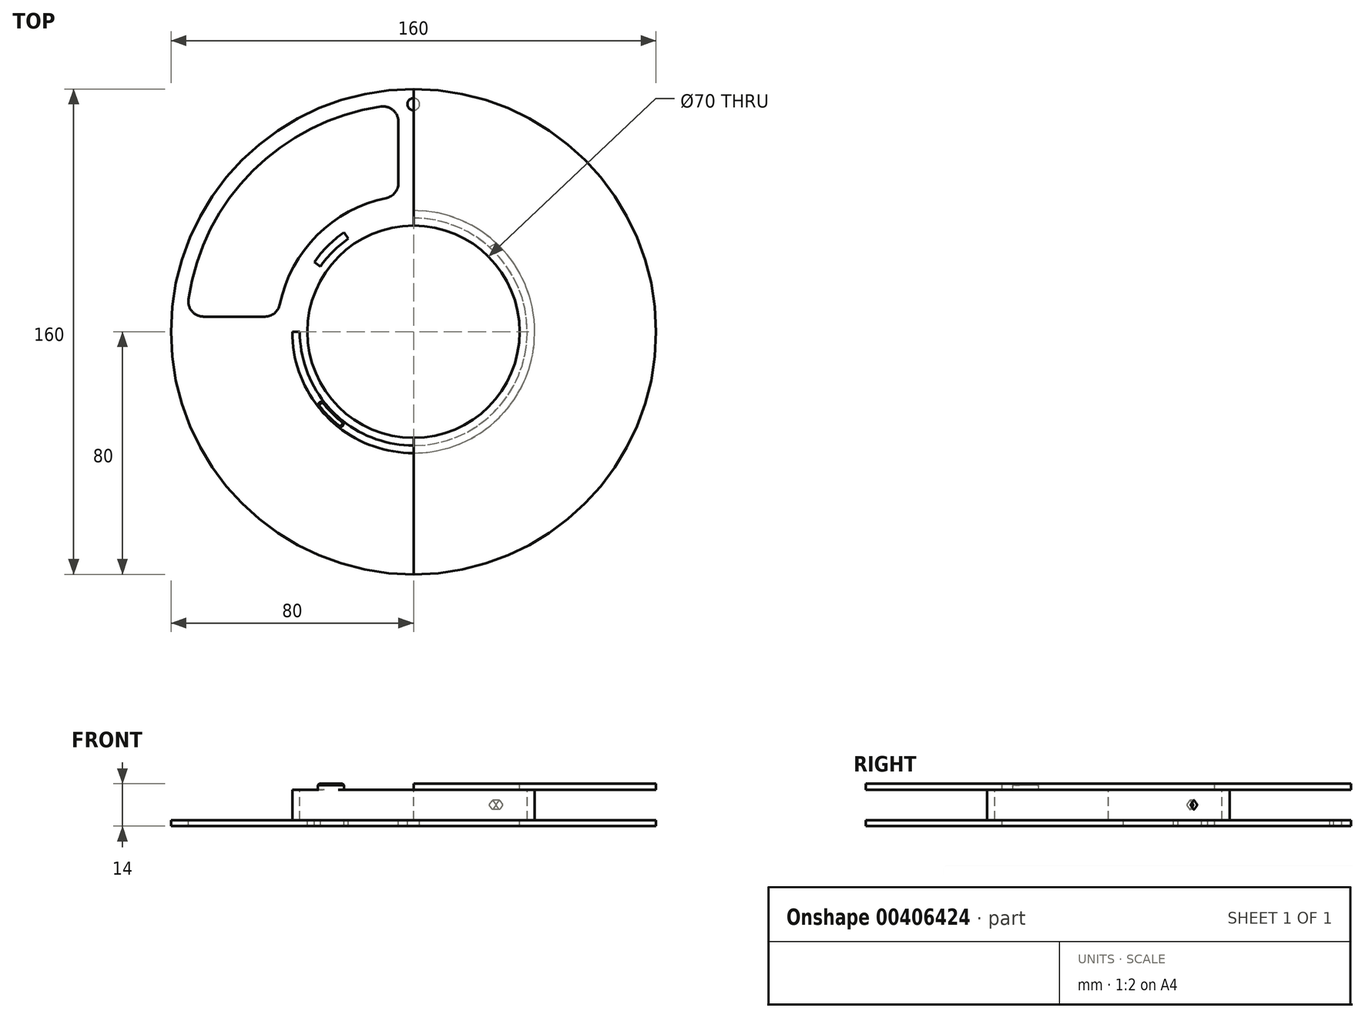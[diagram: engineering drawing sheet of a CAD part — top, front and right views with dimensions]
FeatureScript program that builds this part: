
annotation { "Feature Type Name" : "Feature", "Feature Type Description" : "" }
export const myFeature = defineFeature(function(context is Context, id is Id, definition is map)
    precondition{}
    {
        {
            var Q0;
            Q0=qCreatedBy(makeId("Front.planeOp"),FACE);
            var sketch = newSketch(context, id + "F0", { "sketchPlane" : qUnion([Q0])});
            skLineSegment(sketch, "E0", {"start": v(0, 7) * mm, "end": v(-80, 7) * mm});
            skLineSegment(sketch, "E1", {"start": v(-80, 7) * mm, "end": v(-80, 5) * mm});
            skLineSegment(sketch, "E2", {"start": v(-80, 5) * mm, "end": v(-40, 5) * mm});
            skLineSegment(sketch, "E3", {"start": v(-40, 5) * mm, "end": v(-40, 0) * mm});
            skLineSegment(sketch, "E4", {"start": v(-37.5, 0) * mm, "end": v(-37.5, 5) * mm});
            skLineSegment(sketch, "E5", {"start": v(-37.5, 5) * mm, "end": v(0, 5) * mm});
            skLineSegment(sketch, "E6", {"start": v(0, 5) * mm, "end": v(0, 7) * mm});
            skLineSegment(sketch, "E7.MirrorCS", {"start": v(-80, -7) * mm, "end": v(-80, -5) * mm});
            skLineSegment(sketch, "E8.MirrorCS", {"start": v(0, -7) * mm, "end": v(-80, -7) * mm});
            skLineSegment(sketch, "E9.MirrorCS", {"start": v(-80, -5) * mm, "end": v(-40, -5) * mm});
            skLineSegment(sketch, "E10.MirrorCS", {"start": v(-40, -5) * mm, "end": v(-40, 0) * mm});
            skLineSegment(sketch, "E11.MirrorCS", {"start": v(-37.5, 0) * mm, "end": v(-37.5, -5) * mm});
            skLineSegment(sketch, "E12.MirrorCS", {"start": v(-37.5, -5) * mm, "end": v(0, -5) * mm});
            skLineSegment(sketch, "E13.MirrorCS", {"start": v(0, -5) * mm, "end": v(0, -7) * mm});
            skLineSegment(sketch, "E14", {"start": v(0, 7) * mm, "end": v(0, -7) * mm, "construction": true});
            skSolve(sketch);
        }
        {
            var Q0;
            Q0 = qSketchRegion(id + "F0", true);
            var Q1;
            Q1=sQuery(id+"F0.wireOp",EDGE,"E14");
            revolve(context, id + "F1", {"entities" : qUnion([Q0]), "axis" : qUnion([Q1]), "revolveType" : RevolveType.FULL});
        }
        {
            var Q0;
            Q0=makeQuery(id+"F1.opRevolve","SWEPT_FACE",FACE,{"disambiguationData":[OSD([sQuery(id+"F0.wireOp",EDGE,"E0")])]});
            var sketch = newSketch(context, id + "F2", { "sketchPlane" : qUnion([Q0])});
            skLineSegment(sketch, "E15", {"start": v(-40, 0) * mm, "end": v(-80, 0) * mm, "construction": true});
            skPoint(sketch, "E16.orphan", {"position": v(80, 0) * mm});
            skPoint(sketch, "E17.0.start.orphan", {"position": v(0, -80) * mm});
            skArc(sketch, "E18.0", {"start": v(0, 40) * mm, "mid": v(-28.28, 28.28) * mm, "end": v(-40, 0) * mm, "construction": true});
            skArc(sketch, "E19.1", {"start": v(-9, 44.1) * mm, "mid": v(-31.82, 31.82) * mm, "end": v(-44.1, 9) * mm});
            skLineSegment(sketch, "E20", {"start": v(0, 80) * mm, "end": v(0, 40) * mm, "construction": true});
            skPoint(sketch, "E21.visualSharp", {"position": v(-44.72, 5) * mm});
            skArc(sketch, "E21.filletArc", {"start": v(-48.99, 5) * mm, "mid": v(-45.83, 6.13) * mm, "end": v(-44.1, 9) * mm});
            skPoint(sketch, "E22.visualSharp", {"position": v(-73.21, 5) * mm});
            skPoint(sketch, "E23.visualSharp", {"position": v(-5, 73.21) * mm});
            skPoint(sketch, "E24.visualSharp", {"position": v(-5, 44.72) * mm});
            skArc(sketch, "E24.filletArc", {"start": v(-9, 44.1) * mm, "mid": v(-6.13, 45.83) * mm, "end": v(-5, 48.99) * mm});
            skArc(sketch, "E25", {"start": v(0, 80) * mm, "mid": v(-56.57, 56.57) * mm, "end": v(-80, 0) * mm, "construction": true});
            skArc(sketch, "E26.0", {"start": v(-10.71, 74.23) * mm, "mid": v(-53.03, 53.03) * mm, "end": v(-74.23, 10.71) * mm});
            skLineSegment(sketch, "E27", {"start": v(-48.99, 5) * mm, "end": v(-69.28, 5) * mm});
            skLineSegment(sketch, "E28", {"start": v(-5, 48.99) * mm, "end": v(-5, 69.28) * mm});
            skArc(sketch, "E29.filletArc", {"start": v(-5, 69.28) * mm, "mid": v(-6.73, 73.06) * mm, "end": v(-10.71, 74.23) * mm});
            skArc(sketch, "E30.filletArc", {"start": v(-74.23, 10.71) * mm, "mid": v(-73.06, 6.73) * mm, "end": v(-69.28, 5) * mm});
            skSolve(sketch);
        }
        {
            var Q0;
            Q0 = qSketchRegion(id + "F2", true);
            extrude(context, id + "F3", {"entities" : qUnion([Q0]), "operationType" : NewBodyOperationType.REMOVE, "endBound" : BoundingType.THROUGH_ALL, "oppositeDirection" : true, "depth" : 25 * mm});
        }
        {
            var Q0;
            Q0=sQuery(id+"F2.wireOp",VERTEX,"E18.0.center");
            var Q1;
            Q1=makeQuery(id+"F1.opRevolve","SWEPT_BODY",BODY,{"disambiguationData":[OSD([sQuery(id+"F0.wireOp",EDGE,"E0"),sQuery(id+"F0.wireOp",EDGE,"E1"),sQuery(id+"F0.wireOp",EDGE,"E2"),sQuery(id+"F0.wireOp",EDGE,"E3"),sQuery(id+"F0.wireOp",EDGE,"E4"),sQuery(id+"F0.wireOp",EDGE,"E5"),sQuery(id+"F0.wireOp",EDGE,"E6"),sQuery(id+"F0.wireOp",EDGE,"E7.MirrorCS"),sQuery(id+"F0.wireOp",EDGE,"E8.MirrorCS"),sQuery(id+"F0.wireOp",EDGE,"E9.MirrorCS"),sQuery(id+"F0.wireOp",EDGE,"E10.MirrorCS"),sQuery(id+"F0.wireOp",EDGE,"E11.MirrorCS"),sQuery(id+"F0.wireOp",EDGE,"E12.MirrorCS"),sQuery(id+"F0.wireOp",EDGE,"E13.MirrorCS")])]});
            hole(context, id + "F4", {"style" : HoleStyle.SIMPLE, "endStyle" : HoleEndStyle.THROUGH, "holeDiameter" : 70 * mm, "isTappedThrough" : true, "tappedDepth" : 38.4 * mm, "tapClearance" : 3, "locations" : qUnion([Q0]), "scope" : qUnion([Q1])});
        }
        {
            var Q0;
            Q0=makeQuery(id+"F2.imprint","IMPRINT",FACE,{"disambiguationData":[TD([[makeQuery(id+"F2.imprint","IMPRINT",EDGE,{"derivedFrom":sQuery(id+"F2.wireOp",EDGE,"E19.1")}),1.0]])]});
            var sketch = newSketch(context, id + "F5", { "sketchPlane" : qUnion([Q0])});
            skLineSegment(sketch, "E31", {"start": v(0, 80) * mm, "end": v(0, 0) * mm});
            skLineSegment(sketch, "E32", {"start": v(0, 0) * mm, "end": v(-80, 0) * mm});
            skLineSegment(sketch, "E33", {"start": v(-80, 0) * mm, "end": v(-80, 80) * mm});
            skLineSegment(sketch, "E34", {"start": v(-80, 80) * mm, "end": v(0, 80) * mm});
            skSolve(sketch);
        }
        {
            var Q0;
            Q0 = qSketchRegion(id + "F5", true);
            var Q1;
            Q1=makeQuery(id+"F1.opRevolve","SWEPT_FACE",FACE,{"disambiguationData":[OSD([sQuery(id+"F0.wireOp",EDGE,"E9.MirrorCS")])]});
            extrude(context, id + "F6", {"entities" : qUnion([Q0]), "operationType" : NewBodyOperationType.REMOVE, "endBound" : BoundingType.UP_TO_SURFACE, "oppositeDirection" : true, "endBoundEntityFace" : qUnion([Q1]), "depth" : 25 * mm});
        }
        {
            var Q0;
            Q0=qCreatedBy(makeId("Right.planeOp"),FACE);
            var sketch = newSketch(context, id + "F7", { "sketchPlane" : qUnion([Q0])});
            skPoint(sketch, "E35.0", {"position": v(80, 7) * mm});
            skPoint(sketch, "E36.0", {"position": v(-80, 5) * mm});
            skLineSegment(sketch, "E37.bottom", {"start": v(-80, 5) * mm, "end": v(80, 5) * mm, "construction": true});
            skLineSegment(sketch, "E37.top", {"start": v(-80, 7) * mm, "end": v(80, 7) * mm, "construction": true});
            skLineSegment(sketch, "E37.left", {"start": v(-80, 5) * mm, "end": v(-80, 7) * mm, "construction": true});
            skLineSegment(sketch, "E37.right", {"start": v(80, 5) * mm, "end": v(80, 7) * mm, "construction": true});
            skLineSegment(sketch, "E38.bottom", {"start": v(80, 7) * mm, "end": v(-80, 7) * mm});
            skLineSegment(sketch, "E38.top", {"start": v(80, 5) * mm, "end": v(-80, 5) * mm});
            skLineSegment(sketch, "E38.left", {"start": v(80, 7) * mm, "end": v(80, 5) * mm});
            skLineSegment(sketch, "E38.right", {"start": v(-80, 7) * mm, "end": v(-80, 5) * mm});
            skSolve(sketch);
        }
        {
            var Q0;
            Q0 = qSketchRegion(id + "F7", true);
            extrude(context, id + "F8", {"entities" : qUnion([Q0]), "operationType" : NewBodyOperationType.REMOVE, "endBound" : BoundingType.THROUGH_ALL, "oppositeDirection" : true, "depth" : 25 * mm});
        }
        {
            var Q0;
            {var subQ0=sQuery(id+"F0.wireOp",EDGE,"E12.MirrorCS");var subQ1=sQuery(id+"F0.wireOp",EDGE,"E9.MirrorCS");Q0=makeQuery(id+"F5vmHWThCkjWJyu_1.1.F6.boolean.opBoolean","MERGE",FACE,{"derivedFrom":[makeQuery(id+"F6.boolean.opBoolean","MERGE",FACE,{"derivedFrom":[makeQuery(id+"F1.opRevolve","SWEPT_FACE",FACE,{"disambiguationData":[OSD([subQ1])]}),makeQuery(id+"F1.opRevolve","SWEPT_FACE",FACE,{"disambiguationData":[OSD([subQ0])]}),makeQuery(id+"F6.opExtrude","CAP_FACE",FACE,{"disambiguationData":[OSD([subQ1])],"isStart":false})]}),makeQuery(id+"F5vmHWThCkjWJyu_1.1.F6.opExtrude","CAP_FACE",FACE,{"disambiguationData":[OSD([subQ1,subQ0])],"isStart":false})]});}
            var sketch = newSketch(context, id + "F9", { "sketchPlane" : qUnion([Q0])});
            skArc(sketch, "E39.0", {"start": v(0, 40) * mm, "mid": v(-28.28, 28.28) * mm, "end": v(-40, 0) * mm, "construction": true});
            skLineSegment(sketch, "E40", {"start": v(0, 0) * mm, "end": v(-28.28, 28.28) * mm, "construction": true});
            skArc(sketch, "E41", {"start": v(-28.28, 28.28) * mm, "mid": v(-25.71, 30.64) * mm, "end": v(-22.94, 32.77) * mm});
            skArc(sketch, "E42.0", {"start": v(37.5, 0) * mm, "mid": v(26.52, 26.52) * mm, "end": v(0, 37.5) * mm, "construction": true});
            skArc(sketch, "E43", {"start": v(0, 37.5) * mm, "mid": v(-26.52, 26.52) * mm, "end": v(-37.5, 0) * mm, "construction": true});
            skLineSegment(sketch, "E44", {"start": v(-22.94, 32.77) * mm, "end": v(0, 0) * mm, "construction": true});
            skArc(sketch, "E45", {"start": v(-26.52, 26.52) * mm, "mid": v(-24.1, 28.73) * mm, "end": v(-21.5, 30.72) * mm});
            skArc(sketch, "E46.MirrorCS", {"start": v(-37.5, 0) * mm, "mid": v(-26.52, 26.52) * mm, "end": v(0, 37.5) * mm, "construction": true});
            skArc(sketch, "E47.MirrorCS", {"start": v(-40, 0) * mm, "mid": v(-28.28, 28.28) * mm, "end": v(0, 40) * mm, "construction": true});
            skArc(sketch, "E48", {"start": v(-32.77, 22.94) * mm, "mid": v(-30.64, 25.71) * mm, "end": v(-28.28, 28.28) * mm});
            skLineSegment(sketch, "E49", {"start": v(-32.77, 22.94) * mm, "end": v(0, 0) * mm, "construction": true});
            skArc(sketch, "E50", {"start": v(-30.72, 21.5) * mm, "mid": v(-28.73, 24.1) * mm, "end": v(-26.52, 26.52) * mm});
            skLineSegment(sketch, "E51", {"start": v(-30.72, 21.5) * mm, "end": v(-32.77, 22.94) * mm});
            skLineSegment(sketch, "E52", {"start": v(-22.94, 32.77) * mm, "end": v(-21.5, 30.72) * mm});
            skSolve(sketch);
        }
        {
            var Q0;
            Q0 = qSketchRegion(id + "F9", true);
            extrude(context, id + "F10", {"entities" : qUnion([Q0]), "operationType" : NewBodyOperationType.REMOVE, "endBound" : BoundingType.THROUGH_ALL, "oppositeDirection" : true, "depth" : 25 * mm});
        }
        {
            var Q0;
            Q0=makeQuery(id+"F2.imprint","IMPRINT",FACE,{"disambiguationData":[TD([[makeQuery(id+"F2.imprint","IMPRINT",EDGE,{"derivedFrom":sQuery(id+"F2.wireOp",EDGE,"E19.1")}),1.0]])]});
            var sketch = newSketch(context, id + "F11", { "sketchPlane" : qUnion([Q0])});
            skArc(sketch, "E53.0", {"start": v(-37.5, 0) * mm, "mid": v(-26.52, -26.52) * mm, "end": v(0, -37.5) * mm, "construction": true});
            skArc(sketch, "E54.0", {"start": v(-40, 0) * mm, "mid": v(-28.28, -28.28) * mm, "end": v(0, -40) * mm, "construction": true});
            skLineSegment(sketch, "E55", {"start": v(-28.28, -28.28) * mm, "end": v(0, 0) * mm, "construction": true});
            skLineSegment(sketch, "E56", {"start": v(-24.07, -31.95) * mm, "end": v(0, 0) * mm, "construction": true});
            skLineSegment(sketch, "E57", {"start": v(-31.95, -24.07) * mm, "end": v(0, 0) * mm, "construction": true});
            skArc(sketch, "E58", {"start": v(-24.07, -31.95) * mm, "mid": v(-28.28, -28.28) * mm, "end": v(-31.95, -24.07) * mm});
            skArc(sketch, "E59", {"start": v(-22.57, -29.95) * mm, "mid": v(-26.52, -26.52) * mm, "end": v(-29.95, -22.57) * mm});
            skLineSegment(sketch, "E60", {"start": v(-31.95, -24.07) * mm, "end": v(-29.95, -22.57) * mm});
            skLineSegment(sketch, "E61", {"start": v(-22.57, -29.95) * mm, "end": v(-24.07, -31.95) * mm});
            skSolve(sketch);
        }
        {
            var Q0;
            Q0 = qSketchRegion(id + "F11", true);
            var Q1;
            Q1=makeQuery(id+"F8.boolean.opBoolean","COPY",FACE,{"derivedFrom":makeQuery(id+"F8.opExtrude","SWEPT_FACE",FACE,{"disambiguationData":[OSD([sQuery(id+"F7.wireOp",EDGE,"E38.top")])]})});
            extrude(context, id + "F12", {"entities" : qUnion([Q0]), "operationType" : NewBodyOperationType.ADD, "endBound" : BoundingType.UP_TO_SURFACE, "oppositeDirection" : true, "endBoundEntityFace" : qUnion([Q1]), "depth" : 25 * mm});
        }
        {
            var Q0;
            Q0=makeQuery(id+"F12.opExtrude","SWEPT_EDGE",EDGE,{"disambiguationData":[OSD([sQuery(id+"F11.wireOp",EDGE,"E58"),sQuery(id+"F11.wireOp",EDGE,"E60")])]});
            var Q1;
            Q1=makeQuery(id+"F12.opExtrude","SWEPT_EDGE",EDGE,{"disambiguationData":[OSD([sQuery(id+"F11.wireOp",EDGE,"E58"),sQuery(id+"F11.wireOp",EDGE,"E61")])]});
            var Q2;
            Q2=makeQuery(id+"F12.opExtrude","SWEPT_EDGE",EDGE,{"disambiguationData":[OSD([sQuery(id+"F11.wireOp",EDGE,"E59"),sQuery(id+"F11.wireOp",EDGE,"E60")])]});
            var Q3;
            Q3=makeQuery(id+"F12.opExtrude","SWEPT_EDGE",EDGE,{"disambiguationData":[OSD([sQuery(id+"F11.wireOp",EDGE,"E59"),sQuery(id+"F11.wireOp",EDGE,"E61")])]});
            fillet(context, id + "F13", {"entities" : qUnion([Q0, Q1, Q2, Q3]), "radius" : 1 * mm, "tangentPropagation" : true, "allowEdgeOverflow" : false});
        }
        {
            var Q0;
            Q0=makeQuery(id+"F12.opExtrude","CAP_EDGE",EDGE,{"disambiguationData":[OSD([sQuery(id+"F11.wireOp",EDGE,"E58")])],"isStart":true});
            var Q1;
            Q1=makeQuery(id+"F12.opExtrude","CAP_EDGE",EDGE,{"disambiguationData":[OSD([sQuery(id+"F11.wireOp",EDGE,"E59")])],"isStart":true});
            var Q2;
            Q2=makeQuery(id+"F12.opExtrude","CAP_EDGE",EDGE,{"disambiguationData":[OSD([sQuery(id+"F11.wireOp",EDGE,"E61")])],"isStart":true});
            var Q3;
            Q3=makeQuery(id+"F12.opExtrude","CAP_EDGE",EDGE,{"disambiguationData":[OSD([sQuery(id+"F11.wireOp",EDGE,"E60")])],"isStart":true});
            var Q4;
            Q4=makeQuery(id+"F10.boolean.opBoolean","COPY",EDGE,{"derivedFrom":makeQuery(id+"F10.opExtrude","CAP_EDGE",EDGE,{"disambiguationData":[OSD([sQuery(id+"F9.wireOp",EDGE,"E45"),sQuery(id+"F9.wireOp",EDGE,"E50")])],"isStart":true})});
            var Q5;
            Q5=makeQuery(id+"F10.boolean.opBoolean","COPY",EDGE,{"derivedFrom":makeQuery(id+"F10.opExtrude","CAP_EDGE",EDGE,{"disambiguationData":[OSD([sQuery(id+"F9.wireOp",EDGE,"E51")])],"isStart":true})});
            var Q6;
            Q6=makeQuery(id+"F10.boolean.opBoolean","COPY",EDGE,{"derivedFrom":makeQuery(id+"F10.opExtrude","CAP_EDGE",EDGE,{"disambiguationData":[OSD([sQuery(id+"F9.wireOp",EDGE,"E41"),sQuery(id+"F9.wireOp",EDGE,"E48")])],"isStart":true})});
            var Q7;
            Q7=makeQuery(id+"F10.boolean.opBoolean","COPY",EDGE,{"derivedFrom":makeQuery(id+"F10.opExtrude","CAP_EDGE",EDGE,{"disambiguationData":[OSD([sQuery(id+"F9.wireOp",EDGE,"E52")])],"isStart":true})});
            chamfer(context, id + "F14", {"entities" : qUnion([Q0, Q1, Q2, Q3, Q4, Q5, Q6, Q7]), "width" : .5 * mm, "tangentPropagation" : true});
        }
        {
            var Q0;
            Q0=sQuery(id+"F0.wireOp",EDGE,"E14");
            var Q1;
            Q1=qCreatedBy(makeId("Right.planeOp"),FACE);
            cPlane(context, id + "F15", {"entities" : qUnion([Q0, Q1]), "cplaneType" : CPlaneType.LINE_ANGLE, "offset" : 25 * mm, "angle" : 330 * degree, "width" : 150 * mm, "height" : 150 * mm});
        }
        {
            var Q0;
            Q0=qCreatedBy(id+"F15.planeOp",FACE);
            var sketch = newSketch(context, id + "F16", { "sketchPlane" : qUnion([Q0])});
            skLineSegment(sketch, "E62", {"start": v(-11.51, 0.35) * mm, "end": v(-10.42, 1.44) * mm});
            skLineSegment(sketch, "E63", {"start": v(-10.14, 1.44) * mm, "end": v(-9.05, 0.35) * mm});
            skLineSegment(sketch, "E64", {"start": v(-9.05, -0.35) * mm, "end": v(-10.14, -1.44) * mm});
            skLineSegment(sketch, "E65", {"start": v(-10.42, -1.44) * mm, "end": v(-11.51, -0.35) * mm});
            skPoint(sketch, "E66.visualSharp", {"position": v(-11.87, 0) * mm});
            skArc(sketch, "E66.filletArc", {"start": v(-11.51, 0.35) * mm, "mid": v(-11.66, 0) * mm, "end": v(-11.51, -0.35) * mm});
            skPoint(sketch, "E67.visualSharp", {"position": v(-10.28, -1.59) * mm});
            skArc(sketch, "E67.filletArc", {"start": v(-10.42, -1.44) * mm, "mid": v(-10.28, -1.5) * mm, "end": v(-10.14, -1.44) * mm});
            skPoint(sketch, "E68.visualSharp", {"position": v(-8.7, 0) * mm});
            skArc(sketch, "E68.filletArc", {"start": v(-9.05, -0.35) * mm, "mid": v(-8.9, 0) * mm, "end": v(-9.05, 0.35) * mm});
            skPoint(sketch, "E69.visualSharp", {"position": v(-10.28, 1.59) * mm});
            skArc(sketch, "E69.filletArc", {"start": v(-10.14, 1.44) * mm, "mid": v(-10.28, 1.5) * mm, "end": v(-10.42, 1.44) * mm});
            skSolve(sketch);
        }
        {
            var Q0;
            Q0=makeQuery(id+"F16.imprint","IMPRINT",FACE,{"disambiguationData":[TD([[makeQuery(id+"F16.imprint","IMPRINT",EDGE,{"derivedFrom":sQuery(id+"F16.wireOp",EDGE,"E62")}),-1.0]])]});
            extrude(context, id + "F17", {"entities" : qUnion([Q0]), "operationType" : NewBodyOperationType.REMOVE, "endBound" : BoundingType.THROUGH_ALL, "oppositeDirection" : true, "depth" : 25 * mm});
        }
        {
            var Q0;
            Q0=qCreatedBy(makeId("Top.planeOp"),FACE);
            var sketch = newSketch(context, id + "F18", { "sketchPlane" : qUnion([Q0])});
            skLineSegment(sketch, "E70", {"start": v(0, 87.17) * mm, "end": v(0, 0) * mm, "construction": true});
            skPoint(sketch, "E71", {"position": v(0, 75) * mm});
            skSolve(sketch);
        }
        {
            var Q0;
            Q0=sQuery(id+"F18.wireOp",VERTEX,"E71");
            var Q1;
            Q1=makeQuery(id+"F1.opRevolve","SWEPT_BODY",BODY,{"disambiguationData":[OSD([sQuery(id+"F0.wireOp",EDGE,"E0"),sQuery(id+"F0.wireOp",EDGE,"E1"),sQuery(id+"F0.wireOp",EDGE,"E2"),sQuery(id+"F0.wireOp",EDGE,"E3"),sQuery(id+"F0.wireOp",EDGE,"E4"),sQuery(id+"F0.wireOp",EDGE,"E5"),sQuery(id+"F0.wireOp",EDGE,"E6"),sQuery(id+"F0.wireOp",EDGE,"E7.MirrorCS"),sQuery(id+"F0.wireOp",EDGE,"E8.MirrorCS"),sQuery(id+"F0.wireOp",EDGE,"E9.MirrorCS"),sQuery(id+"F0.wireOp",EDGE,"E10.MirrorCS"),sQuery(id+"F0.wireOp",EDGE,"E11.MirrorCS"),sQuery(id+"F0.wireOp",EDGE,"E12.MirrorCS"),sQuery(id+"F0.wireOp",EDGE,"E13.MirrorCS")])]});
            hole(context, id + "F19", {"style" : HoleStyle.SIMPLE, "endStyle" : HoleEndStyle.THROUGH, "holeDiameter" : 4 * mm, "isTappedThrough" : true, "tappedDepth" : 38.4 * mm, "tapClearance" : 3, "locations" : qUnion([Q0]), "scope" : qUnion([Q1])});
        }
    });
